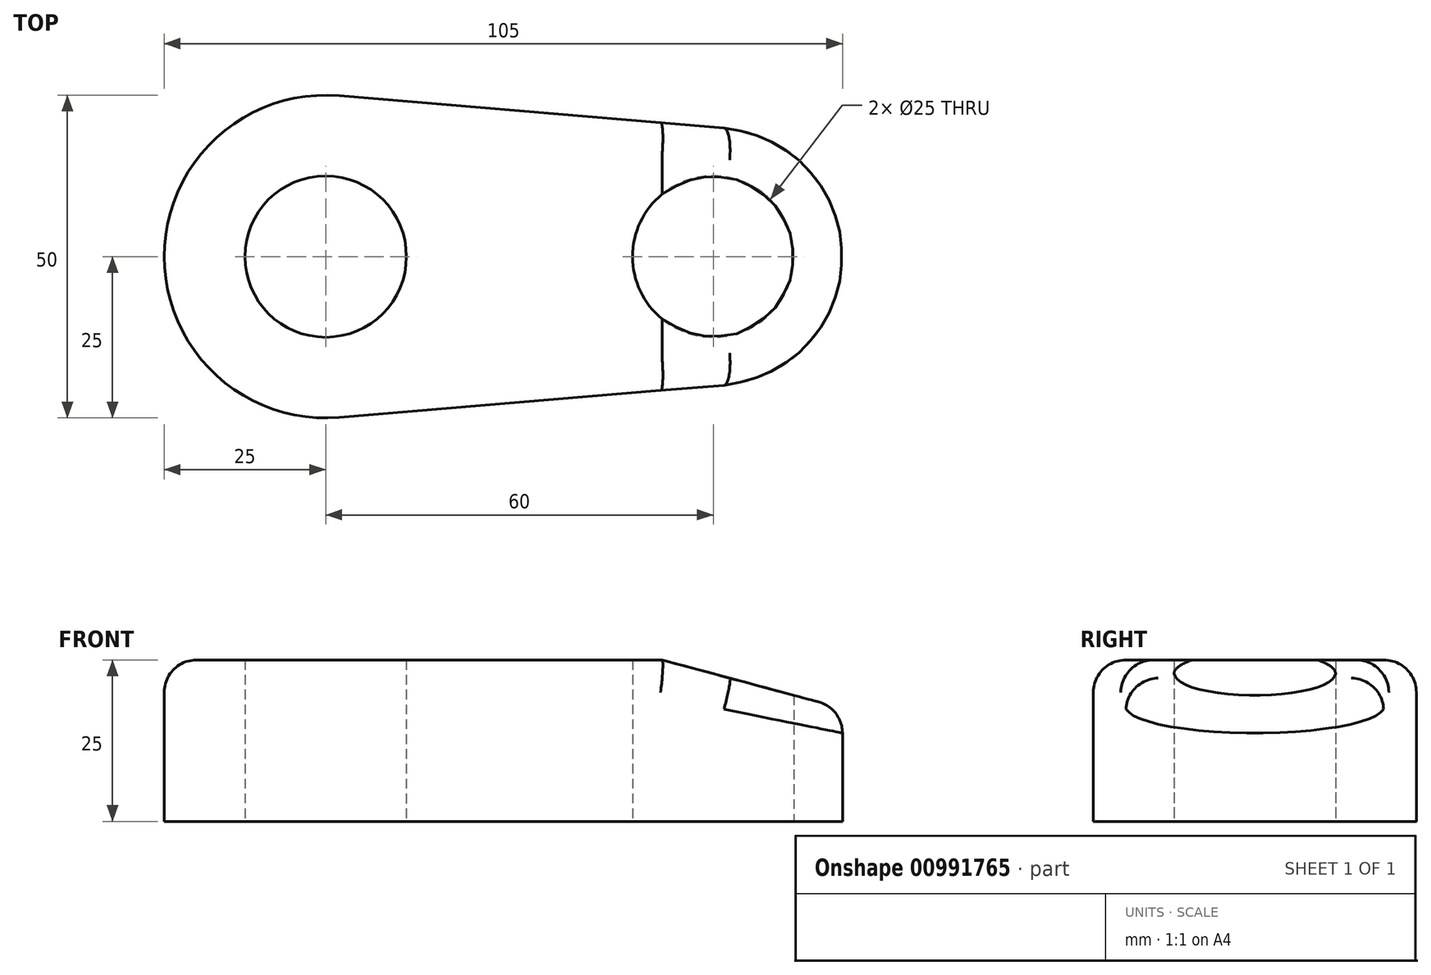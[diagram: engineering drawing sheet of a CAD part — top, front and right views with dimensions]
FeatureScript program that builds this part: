
annotation { "Feature Type Name" : "Feature", "Feature Type Description" : "" }
export const myFeature = defineFeature(function(context is Context, id is Id, definition is map)
    precondition{}
    {
        {
            var Q0;
            Q0=qCreatedBy(makeId("Top.planeOp"),FACE);
            var sketch = newSketch(context, id + "F0", { "sketchPlane" : qUnion([Q0])});
            skCircle(sketch, "E0", {"center": v(0, 0) * mm, "radius": 12.5 * mm});
            skCircle(sketch, "E1", {"center": v(60, 0) * mm, "radius": 12.5 * mm});
            skCircle(sketch, "E2", {"center": v(0, 0) * mm, "radius": 25 * mm});
            skCircle(sketch, "E3", {"center": v(60, 0) * mm, "radius": 20 * mm});
            skLineSegment(sketch, "E4", {"start": v(2.08, 24.91) * mm, "end": v(61.67, 19.93) * mm});
            skLineSegment(sketch, "E5", {"start": v(2.08, -24.91) * mm, "end": v(61.67, -19.93) * mm});
            skSolve(sketch);
        }
        {
            var Q0;
            Q0=makeQuery(id+"F0.imprint","IMPRINT",FACE,{"disambiguationData":[TD([[makeQuery(id+"F0.imprint","IMPRINT",EDGE,{"derivedFrom":sQuery(id+"F0.wireOp",EDGE,"E0")}),-1.0]])]});
            var Q1;
            {var subQ0=sQuery(id+"F0.wireOp",EDGE,"E4");Q1=makeQuery(id+"F0.imprint","IMPRINT",FACE,{"disambiguationData":[TD([[makeQuery(id+"F0.imprint","IMPRINT",EDGE,{"derivedFrom":subQ0}),-1.0]])]});}
            var Q2;
            Q2=makeQuery(id+"F0.imprint","IMPRINT",FACE,{"disambiguationData":[TD([[makeQuery(id+"F0.imprint","IMPRINT",EDGE,{"derivedFrom":sQuery(id+"F0.wireOp",EDGE,"E1")}),-1.0]])]});
            extrude(context, id + "F1", {"entities" : qUnion([Q0, Q1, Q2]), "depth" : 25 * mm, "offsetDistance" : 25 * mm});
        }
        {
            var Q0;
            Q0=qCreatedBy(makeId("Front.planeOp"),FACE);
            var sketch = newSketch(context, id + "F2", { "sketchPlane" : qUnion([Q0])});
            skLineSegment(sketch, "E6", {"start": v(52.08, 25) * mm, "end": v(80, 25) * mm});
            skLineSegment(sketch, "E7", {"start": v(80, 25) * mm, "end": v(80, 17.52) * mm});
            skLineSegment(sketch, "E8", {"start": v(80, 17.52) * mm, "end": v(52.08, 25) * mm});
            skLineSegment(sketch, "E9.0", {"start": v(2.08, 25) * mm, "end": v(61.67, 25) * mm});
            skLineSegment(sketch, "E10", {"start": v(80, 25) * mm, "end": v(80, 0) * mm});
            skSolve(sketch);
        }
        {
            var Q0;
            Q0 = qSketchRegion(id + "F2", true);
            extrude(context, id + "F3", {"entities" : qUnion([Q0]), "operationType" : NewBodyOperationType.REMOVE, "endBound" : BoundingType.SYMMETRIC, "oppositeDirection" : true, "depth" : 50 * mm, "offsetDistance" : 25 * mm});
        }
        {
            var Q0;
            Q0=makeQuery(id+"F1.opExtrude","CAP_EDGE",EDGE,{"disambiguationData":[OSD([sQuery(id+"F0.wireOp",EDGE,"E5")])],"isStart":false});
            var Q1;
            Q1=makeQuery(id+"F3.boolean.opBoolean","INTERSECT",EDGE,{"derivedFrom":[makeQuery(id+"F1.opExtrude","SWEPT_FACE",FACE,{"disambiguationData":[OSD([sQuery(id+"F0.wireOp",EDGE,"E3")])]}),makeQuery(id+"F3.opExtrude","SWEPT_FACE",FACE,{"disambiguationData":[OSD([sQuery(id+"F2.wireOp",EDGE,"E8")])]})]});
            var Q2;
            Q2=makeQuery(id+"F3.boolean.opBoolean","INTERSECT",EDGE,{"derivedFrom":[makeQuery(id+"F1.opExtrude","SWEPT_FACE",FACE,{"disambiguationData":[OSD([sQuery(id+"F0.wireOp",EDGE,"E5")])]}),makeQuery(id+"F3.opExtrude","SWEPT_FACE",FACE,{"disambiguationData":[OSD([sQuery(id+"F2.wireOp",EDGE,"E8")])]})]});
            var Q3;
            Q3=makeQuery(id+"F3.boolean.opBoolean","INTERSECT",EDGE,{"derivedFrom":[makeQuery(id+"F1.opExtrude","SWEPT_FACE",FACE,{"disambiguationData":[OSD([sQuery(id+"F0.wireOp",EDGE,"E4")])]}),makeQuery(id+"F3.opExtrude","SWEPT_FACE",FACE,{"disambiguationData":[OSD([sQuery(id+"F2.wireOp",EDGE,"E8")])]})]});
            fillet(context, id + "F4", {"entities" : qUnion([Q0, Q1, Q2, Q3]), "radius" : 5 * mm, "tangentPropagation" : true, "allowEdgeOverflow" : false});
        }
    });
